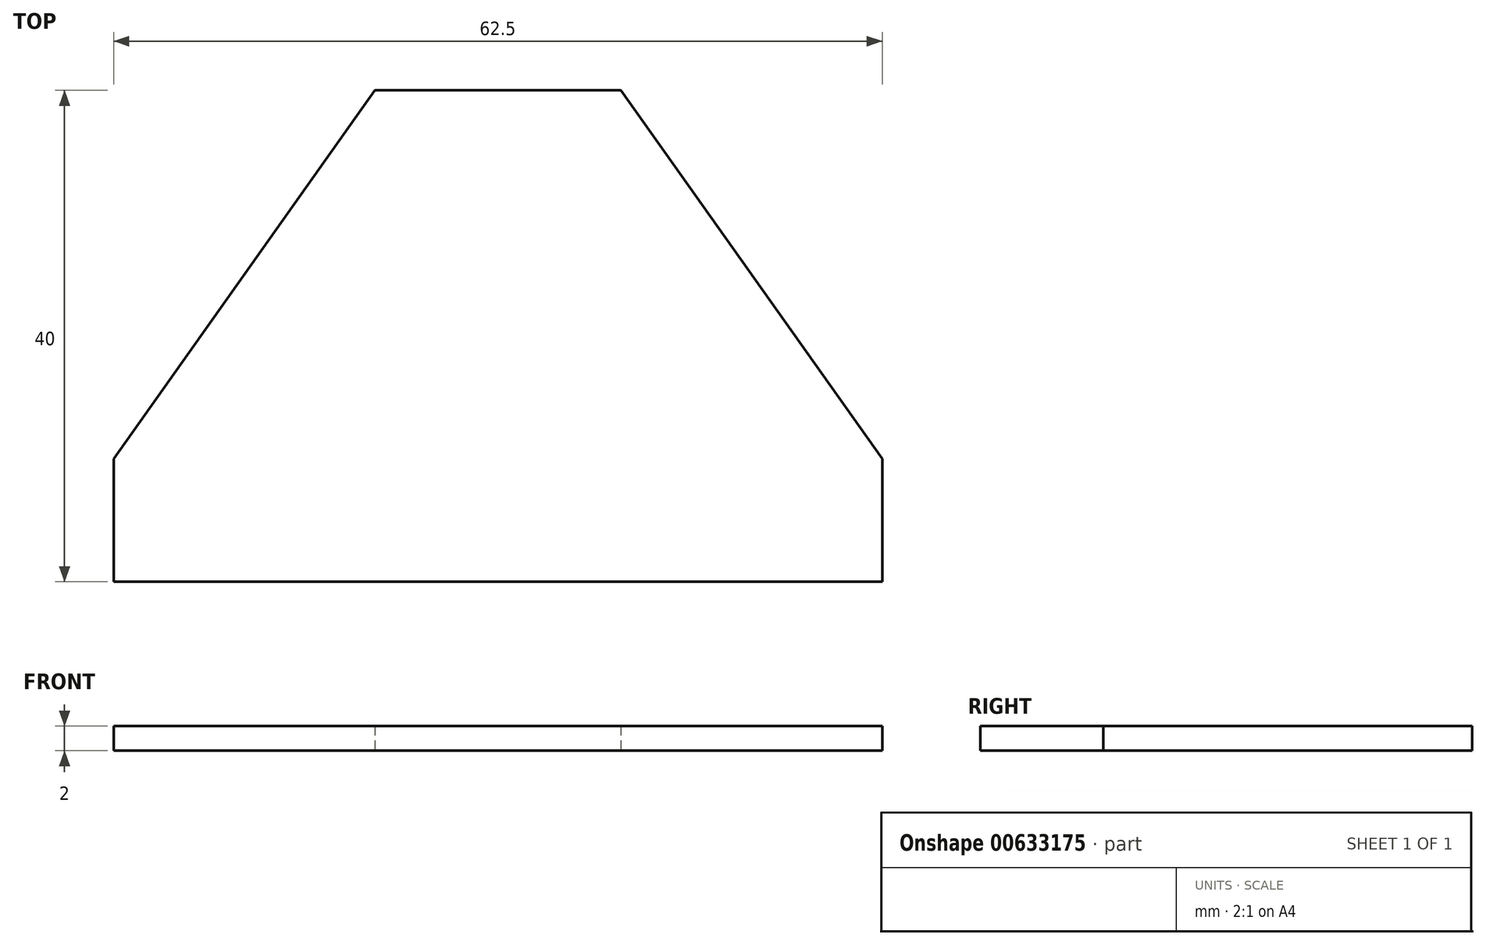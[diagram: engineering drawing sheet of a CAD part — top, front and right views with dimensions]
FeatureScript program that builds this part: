
annotation { "Feature Type Name" : "Feature", "Feature Type Description" : "" }
export const myFeature = defineFeature(function(context is Context, id is Id, definition is map)
    precondition{}
    {
        {
            var Q0;
            Q0=qCreatedBy(makeId("Top.planeOp"),FACE);
            var sketch = newSketch(context, id + "F0", { "sketchPlane" : qUnion([Q0])});
            skLineSegment(sketch, "E0", {"start": v(0, 0) * mm, "end": v(-62.5, 0) * mm});
            skLineSegment(sketch, "E1", {"start": v(-62.5, 0) * mm, "end": v(-62.5, 10) * mm});
            skLineSegment(sketch, "E2", {"start": v(-62.5, 10) * mm, "end": v(-41.25, 40) * mm});
            skLineSegment(sketch, "E3", {"start": v(-41.25, 40) * mm, "end": v(-21.25, 40) * mm});
            skLineSegment(sketch, "E4", {"start": v(-21.25, 40) * mm, "end": v(0, 10) * mm});
            skLineSegment(sketch, "E5", {"start": v(0, 10) * mm, "end": v(0, 0) * mm});
            skSolve(sketch);
        }
        {
            var Q0;
            Q0=makeQuery(id+"F0.imprint","IMPRINT",FACE,{"disambiguationData":[TD([[makeQuery(id+"F0.imprint","IMPRINT",EDGE,{"derivedFrom":sQuery(id+"F0.wireOp",EDGE,"E0")}),-1.0]])]});
            extrude(context, id + "F1", {"entities" : qUnion([Q0]), "depth" : 2 * mm, "offsetDistance" : 25 * mm});
        }
    });
